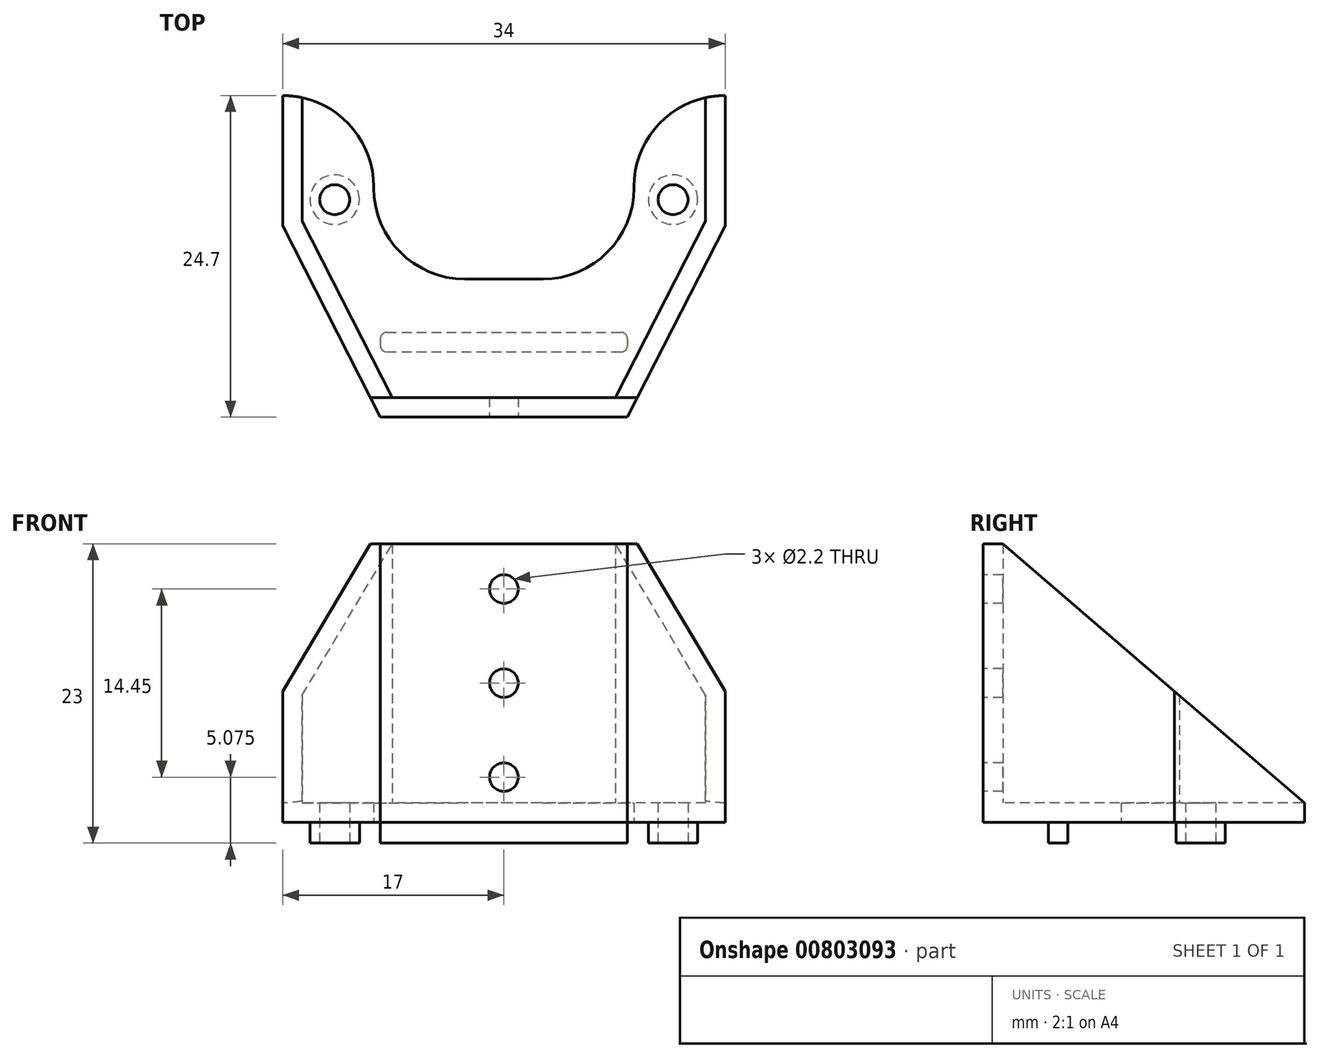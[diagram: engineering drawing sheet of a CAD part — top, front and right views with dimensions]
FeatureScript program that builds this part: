
annotation { "Feature Type Name" : "Feature", "Feature Type Description" : "" }
export const myFeature = defineFeature(function(context is Context, id is Id, definition is map)
    precondition{}
    {
        {
            var Q0;
            Q0=qCreatedBy(makeId("Top.planeOp"),FACE);
            var sketch = newSketch(context, id + "F0", { "sketchPlane" : qUnion([Q0])});
            skLineSegment(sketch, "E0", {"start": v(-15, -8.1) * mm, "end": v(15, -8.1) * mm});
            skLineSegment(sketch, "E1.bottom", {"start": v(-15, 24) * mm, "end": v(-11, 24) * mm});
            skLineSegment(sketch, "E1.top", {"start": v(-15, 0) * mm, "end": v(-11, 0) * mm});
            skLineSegment(sketch, "E1.left", {"start": v(-15, 24) * mm, "end": v(-15, 0) * mm});
            skLineSegment(sketch, "E1.right", {"start": v(-11, 24) * mm, "end": v(-11, 0) * mm});
            skLineSegment(sketch, "E2.MirrorCS", {"start": v(11, 24) * mm, "end": v(11, 0) * mm});
            skLineSegment(sketch, "E3.MirrorCS", {"start": v(15, 24) * mm, "end": v(15, 0) * mm});
            skLineSegment(sketch, "E4.MirrorCS", {"start": v(15, 24) * mm, "end": v(11, 24) * mm});
            skLineSegment(sketch, "E5.MirrorCS", {"start": v(15, 0) * mm, "end": v(11, 0) * mm});
            skSolve(sketch);
        }
        {
            var Q0;
            Q0=qCreatedBy(makeId("Top.planeOp"),FACE);
            var sketch = newSketch(context, id + "F1", { "sketchPlane" : qUnion([Q0])});
            skCircle(sketch, "E6", {"center": v(-13, 2) * mm, "radius": 1.9 * mm});
            skCircle(sketch, "E7.MirrorC", {"center": v(13, 2) * mm, "radius": 1.9 * mm});
            skLineSegment(sketch, "E8.bottom", {"start": v(-9.5, -8.2) * mm, "end": v(9.5, -8.2) * mm});
            skLineSegment(sketch, "E8.top", {"start": v(-9.5, -9.7) * mm, "end": v(9.5, -9.7) * mm});
            skLineSegment(sketch, "E8.left", {"start": v(-9.5, -8.2) * mm, "end": v(-9.5, -9.7) * mm});
            skLineSegment(sketch, "E8.right", {"start": v(9.5, -8.2) * mm, "end": v(9.5, -9.7) * mm});
            skSolve(sketch);
        }
        {
            var Q0;
            Q0=qCreatedBy(makeId("Top.planeOp"),FACE);
            var sketch = newSketch(context, id + "F2", { "sketchPlane" : qUnion([Q0])});
            skLineSegment(sketch, "E9", {"start": v(-9.5, -14.7) * mm, "end": v(-17, 0) * mm});
            skLineSegment(sketch, "E10", {"start": v(-17, 0) * mm, "end": v(-17, 10) * mm});
            skLineSegment(sketch, "E11", {"start": v(-17, 10) * mm, "end": v(-10, 10) * mm});
            skLineSegment(sketch, "E12", {"start": v(-10, 10) * mm, "end": v(-10, -4.1) * mm});
            skLineSegment(sketch, "E13", {"start": v(-10, -4.1) * mm, "end": v(0, -4.1) * mm});
            skLineSegment(sketch, "E14", {"start": v(-9.5, -14.7) * mm, "end": v(0, -14.7) * mm});
            skLineSegment(sketch, "E15.MirrorCS", {"start": v(10, -4.1) * mm, "end": v(0, -4.1) * mm});
            skLineSegment(sketch, "E16.MirrorCS", {"start": v(10, 10) * mm, "end": v(10, -4.1) * mm});
            skLineSegment(sketch, "E17.MirrorCS", {"start": v(17, 10) * mm, "end": v(10, 10) * mm});
            skLineSegment(sketch, "E18.MirrorCS", {"start": v(17, 0) * mm, "end": v(17, 10) * mm});
            skLineSegment(sketch, "E19.MirrorCS", {"start": v(9.5, -14.7) * mm, "end": v(17, 0) * mm});
            skLineSegment(sketch, "E20.MirrorCS", {"start": v(9.5, -14.7) * mm, "end": v(0, -14.7) * mm});
            skSolve(sketch);
        }
        {
            var Q0;
            Q0=makeQuery(id+"F2.imprint","IMPRINT",FACE,{"disambiguationData":[TD([[makeQuery(id+"F2.imprint","IMPRINT",EDGE,{"derivedFrom":sQuery(id+"F2.wireOp",EDGE,"E9")}),-1.0]])]});
            var sketch = newSketch(context, id + "F3", { "sketchPlane" : qUnion([Q0])});
            skLineSegment(sketch, "E21", {"start": v(-17, 10) * mm, "end": v(-17, 0) * mm});
            skLineSegment(sketch, "E22", {"start": v(-17, 0) * mm, "end": v(-9.5, -14.7) * mm});
            skLineSegment(sketch, "E23", {"start": v(-9.5, -14.7) * mm, "end": v(0, -14.7) * mm});
            skLineSegment(sketch, "E24", {"start": v(-17, 10) * mm, "end": v(-15.5, 10) * mm});
            skLineSegment(sketch, "E25", {"start": v(-15.5, 10) * mm, "end": v(-15.5, 0.36) * mm});
            skLineSegment(sketch, "E26", {"start": v(-15.5, 0.36) * mm, "end": v(-8.58, -13.2) * mm});
            skLineSegment(sketch, "E27", {"start": v(-8.58, -13.2) * mm, "end": v(0, -13.2) * mm});
            skPoint(sketch, "E28.orphan", {"position": v(-15.5, 0) * mm});
            skLineSegment(sketch, "E29.MirrorCS", {"start": v(15.5, 10) * mm, "end": v(15.5, 0.36) * mm});
            skLineSegment(sketch, "E30.MirrorCS", {"start": v(17, 10) * mm, "end": v(17, 0) * mm});
            skLineSegment(sketch, "E31.MirrorCS", {"start": v(17, 0) * mm, "end": v(9.5, -14.7) * mm});
            skLineSegment(sketch, "E32.MirrorCS", {"start": v(9.5, -14.7) * mm, "end": v(0, -14.7) * mm});
            skLineSegment(sketch, "E33.MirrorCS", {"start": v(8.58, -13.2) * mm, "end": v(0, -13.2) * mm});
            skLineSegment(sketch, "E34.MirrorCS", {"start": v(15.5, 0.36) * mm, "end": v(8.58, -13.2) * mm});
            skLineSegment(sketch, "E35.MirrorCS", {"start": v(17, 10) * mm, "end": v(15.5, 10) * mm});
            skSolve(sketch);
        }
        {
            var Q0;
            Q0=qSketchRegion(id+"F3",true);
            extrude(context, id + "F4", {"entities" : qUnion([Q0]), "depth" : 21.4 * mm, "offsetDistance" : 25 * mm});
        }
        {
            var Q0;
            Q0=qSketchRegion(id+"F2",true);
            extrude(context, id + "F5", {"entities" : qUnion([Q0]), "operationType" : NewBodyOperationType.ADD, "depth" : 1.5 * mm, "offsetDistance" : 25 * mm});
        }
        {
            var Q0;
            Q0=qSketchRegion(id+"F1",true);
            extrude(context, id + "F6", {"entities" : qUnion([Q0]), "operationType" : NewBodyOperationType.ADD, "oppositeDirection" : true, "depth" : 1.6 * mm, "offsetDistance" : 25 * mm});
        }
        {
            var Q0;
            Q0=qCreatedBy(makeId("Right.planeOp"),FACE);
            var sketch = newSketch(context, id + "F7", { "sketchPlane" : qUnion([Q0])});
            skLineSegment(sketch, "E36", {"start": v(10, 1.5) * mm, "end": v(-13.2, 21.4) * mm});
            skLineSegment(sketch, "E37", {"start": v(-13.2, 21.4) * mm, "end": v(10, 21.4) * mm});
            skLineSegment(sketch, "E38", {"start": v(10, 21.4) * mm, "end": v(10, 1.5) * mm});
            skSolve(sketch);
        }
        {
            var Q0;
            Q0=qSketchRegion(id+"F7",true);
            extrude(context, id + "F8", {"entities" : qUnion([Q0]), "operationType" : NewBodyOperationType.REMOVE, "endBound" : BoundingType.THROUGH_ALL, "oppositeDirection" : true, "depth" : 25 * mm, "offsetDistance" : 25 * mm, "hasSecondDirection" : true, "secondDirectionBound" : SecondDirectionBoundingType.THROUGH_ALL, "secondDirectionOppositeDirection" : false, "secondDirectionDepth" : 25 * mm});
        }
        {
            var Q0;
            Q0=qCreatedBy(makeId("Top.planeOp"),FACE);
            var sketch = newSketch(context, id + "F9", { "sketchPlane" : qUnion([Q0])});
            skCircle(sketch, "E39", {"center": v(13, 2) * mm, "radius": 1.15 * mm});
            skCircle(sketch, "E40.MirrorC", {"center": v(-13, 2) * mm, "radius": 1.15 * mm});
            skSolve(sketch);
        }
        {
            var Q0;
            Q0=qSketchRegion(id+"F9",true);
            extrude(context, id + "F10", {"entities" : qUnion([Q0]), "operationType" : NewBodyOperationType.REMOVE, "endBound" : BoundingType.THROUGH_ALL, "depth" : 25 * mm, "offsetDistance" : 25 * mm, "hasSecondDirection" : true, "secondDirectionBound" : SecondDirectionBoundingType.THROUGH_ALL, "secondDirectionOppositeDirection" : true, "secondDirectionDepth" : 25 * mm});
        }
        {
            var Q0;
            Q0=makeQuery(id+"F4.opExtrude","SWEPT_FACE",FACE,{"disambiguationData":[OSD([sQuery(id+"F3.wireOp",EDGE,"E23"),sQuery(id+"F3.wireOp",EDGE,"E32.MirrorCS")])]});
            var sketch = newSketch(context, id + "F11", { "sketchPlane" : qUnion([Q0])});
            skCircle(sketch, "E41", {"center": v(0, 3.47) * mm, "radius": 1.1 * mm});
            skCircle(sketch, "E42", {"center": v(0, 17.92) * mm, "radius": 1.1 * mm});
            skCircle(sketch, "E43", {"center": v(0, 10.7) * mm, "radius": 1.1 * mm});
            skSolve(sketch);
        }
        {
            var Q0;
            Q0=qSketchRegion(id+"F11",true);
            extrude(context, id + "F12", {"entities" : qUnion([Q0]), "operationType" : NewBodyOperationType.REMOVE, "endBound" : BoundingType.UP_TO_NEXT, "oppositeDirection" : true, "depth" : 25 * mm, "offsetDistance" : 25 * mm});
        }
        {
            var Q0;
            Q0=makeQuery(id+"F5.opExtrude","SWEPT_EDGE",EDGE,{"disambiguationData":[OSD([sQuery(id+"F2.wireOp",EDGE,"E11"),sQuery(id+"F2.wireOp",EDGE,"E12")])]});
            var Q1;
            Q1=makeQuery(id+"F5.opExtrude","SWEPT_EDGE",EDGE,{"disambiguationData":[OSD([sQuery(id+"F2.wireOp",EDGE,"E16.MirrorCS"),sQuery(id+"F2.wireOp",EDGE,"E17.MirrorCS")])]});
            var Q2;
            Q2=makeQuery(id+"F5.opExtrude","SWEPT_EDGE",EDGE,{"disambiguationData":[OSD([sQuery(id+"F2.wireOp",EDGE,"E15.MirrorCS"),sQuery(id+"F2.wireOp",EDGE,"E16.MirrorCS")])]});
            var Q3;
            Q3=makeQuery(id+"F5.opExtrude","SWEPT_EDGE",EDGE,{"disambiguationData":[OSD([sQuery(id+"F2.wireOp",EDGE,"E12"),sQuery(id+"F2.wireOp",EDGE,"E13")])]});
            fillet(context, id + "F13", {"entities" : qUnion([Q0, Q1, Q2, Q3]), "radius" : 7 * mm, "tangentPropagation" : true, "allowEdgeOverflow" : false});
        }
        {
            var Q0;
            Q0=makeQuery(id+"F6.opExtrude","SWEPT_EDGE",EDGE,{"disambiguationData":[OSD([sQuery(id+"F1.wireOp",EDGE,"E8.bottom"),sQuery(id+"F1.wireOp",EDGE,"E8.left")])]});
            var Q1;
            Q1=makeQuery(id+"F6.opExtrude","SWEPT_EDGE",EDGE,{"disambiguationData":[OSD([sQuery(id+"F1.wireOp",EDGE,"E8.top"),sQuery(id+"F1.wireOp",EDGE,"E8.left")])]});
            var Q2;
            Q2=makeQuery(id+"F6.opExtrude","SWEPT_EDGE",EDGE,{"disambiguationData":[OSD([sQuery(id+"F1.wireOp",EDGE,"E8.bottom"),sQuery(id+"F1.wireOp",EDGE,"E8.right")])]});
            var Q3;
            Q3=makeQuery(id+"F6.opExtrude","SWEPT_EDGE",EDGE,{"disambiguationData":[OSD([sQuery(id+"F1.wireOp",EDGE,"E8.top"),sQuery(id+"F1.wireOp",EDGE,"E8.right")])]});
            fillet(context, id + "F14", {"entities" : qUnion([Q0, Q1, Q2, Q3]), "radius" : 0.5 * mm, "tangentPropagation" : true, "allowEdgeOverflow" : false});
        }
    });
